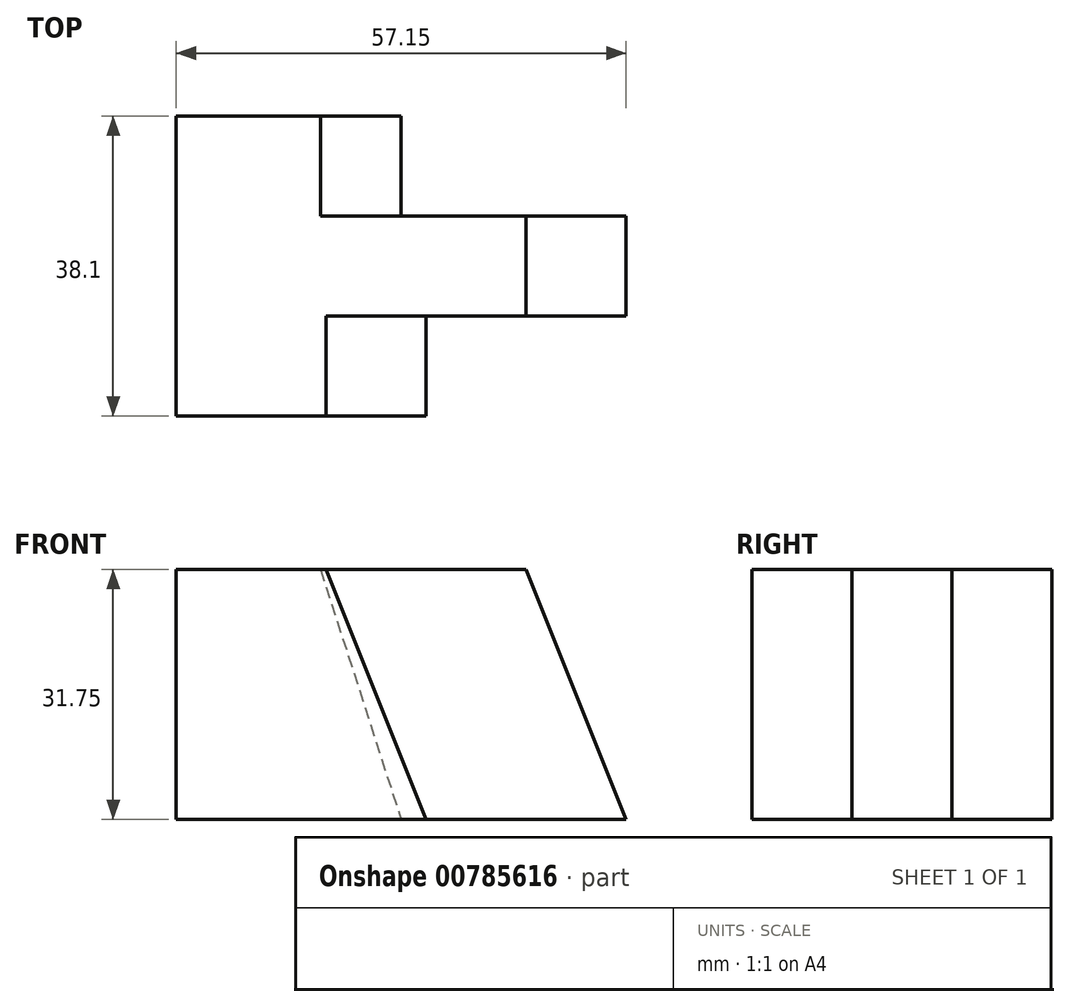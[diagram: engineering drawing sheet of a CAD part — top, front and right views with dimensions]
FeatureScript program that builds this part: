
annotation { "Feature Type Name" : "Feature", "Feature Type Description" : "" }
export const myFeature = defineFeature(function(context is Context, id is Id, definition is map)
    precondition{}
    {
        {
            var Q0;
            Q0=qCreatedBy(makeId("Front.planeOp"),FACE);
            var sketch = newSketch(context, id + "F0", { "sketchPlane" : qUnion([Q0])});
            skLineSegment(sketch, "E0", {"start": v(0, 0) * mm, "end": v(57.15, 0) * mm});
            skLineSegment(sketch, "E1", {"start": v(57.15, 0) * mm, "end": v(57.15, 31.75) * mm});
            skLineSegment(sketch, "E2", {"start": v(57.15, 31.75) * mm, "end": v(0, 31.75) * mm});
            skLineSegment(sketch, "E3", {"start": v(0, 0) * mm, "end": v(0, 31.75) * mm});
            skSolve(sketch);
        }
        {
            var Q0;
            Q0=makeQuery(id+"F0.imprint","IMPRINT",FACE,{"disambiguationData":[TD([[makeQuery(id+"F0.imprint","IMPRINT",EDGE,{"derivedFrom":sQuery(id+"F0.wireOp",EDGE,"E0")}),1.0]])]});
            extrude(context, id + "F1", {"entities" : qUnion([Q0]), "depth" : 38.1 * mm, "offsetDistance" : 25.4 * mm});
        }
        {
            var Q0;
            Q0=makeQuery(id+"F1.opExtrude","CAP_FACE",FACE,{"disambiguationData":[OSD([sQuery(id+"F0.wireOp",EDGE,"E0"),sQuery(id+"F0.wireOp",EDGE,"E1"),sQuery(id+"F0.wireOp",EDGE,"E2"),sQuery(id+"F0.wireOp",EDGE,"E3")])],"isStart":false});
            var sketch = newSketch(context, id + "F2", { "sketchPlane" : qUnion([Q0])});
            skLineSegment(sketch, "E4", {"start": v(19.05, 31.75) * mm, "end": v(31.75, 0) * mm});
            skLineSegment(sketch, "E5", {"start": v(19.05, 31.75) * mm, "end": v(57.15, 31.75) * mm});
            skLineSegment(sketch, "E6", {"start": v(31.75, 0) * mm, "end": v(57.15, 0) * mm});
            skLineSegment(sketch, "E7", {"start": v(57.15, 0) * mm, "end": v(57.15, 31.75) * mm});
            skSolve(sketch);
        }
        {
            var Q0;
            Q0=makeQuery(id+"F2.imprint","IMPRINT",FACE,{"disambiguationData":[TD([[makeQuery(id+"F2.imprint","IMPRINT",EDGE,{"derivedFrom":sQuery(id+"F2.wireOp",EDGE,"E4")}),1.0]])]});
            extrude(context, id + "F3", {"entities" : qUnion([Q0]), "operationType" : NewBodyOperationType.REMOVE, "oppositeDirection" : true, "depth" : 12.7 * mm, "offsetDistance" : 25.4 * mm});
        }
        {
            var Q0;
            Q0=makeQuery(id+"F3.boolean.opBoolean","COPY",FACE,{"derivedFrom":makeQuery(id+"F3.opExtrude","CAP_FACE",FACE,{"disambiguationData":[OSD([sQuery(id+"F2.wireOp",EDGE,"E4"),sQuery(id+"F2.wireOp",EDGE,"E5"),sQuery(id+"F2.wireOp",EDGE,"E6"),sQuery(id+"F2.wireOp",EDGE,"E7")])],"isStart":false})});
            var sketch = newSketch(context, id + "F4", { "sketchPlane" : qUnion([Q0])});
            skLineSegment(sketch, "E8", {"start": v(19.05, 31.75) * mm, "end": v(44.45, 31.75) * mm});
            skLineSegment(sketch, "E9", {"start": v(44.45, 31.75) * mm, "end": v(57.15, 0) * mm});
            skLineSegment(sketch, "E10", {"start": v(57.15, 0) * mm, "end": v(57.15, 31.75) * mm});
            skLineSegment(sketch, "E11", {"start": v(57.15, 31.75) * mm, "end": v(44.45, 31.75) * mm});
            skSolve(sketch);
        }
        {
            var Q0;
            Q0=makeQuery(id+"F4.imprint","IMPRINT",FACE,{"disambiguationData":[TD([[makeQuery(id+"F4.imprint","IMPRINT",EDGE,{"derivedFrom":sQuery(id+"F4.wireOp",EDGE,"E9")}),1.0]])]});
            extrude(context, id + "F5", {"entities" : qUnion([Q0]), "operationType" : NewBodyOperationType.REMOVE, "oppositeDirection" : true, "depth" : 25.4 * mm, "offsetDistance" : 25.4 * mm});
        }
        {
            var Q0;
            Q0=makeQuery(id+"F1.opExtrude","CAP_FACE",FACE,{"disambiguationData":[OSD([sQuery(id+"F0.wireOp",EDGE,"E0"),sQuery(id+"F0.wireOp",EDGE,"E1"),sQuery(id+"F0.wireOp",EDGE,"E2"),sQuery(id+"F0.wireOp",EDGE,"E3")])],"isStart":true});
            var sketch = newSketch(context, id + "F6", { "sketchPlane" : qUnion([Q0])});
            skLineSegment(sketch, "E12", {"start": v(0, 31.75) * mm, "end": v(-18.33, 31.75) * mm});
            skLineSegment(sketch, "E13", {"start": v(-18.33, 31.75) * mm, "end": v(-28.58, 0) * mm});
            skLineSegment(sketch, "E14", {"start": v(-18.33, 31.75) * mm, "end": v(-44.45, 31.75) * mm});
            skLineSegment(sketch, "E15", {"start": v(-44.45, 31.75) * mm, "end": v(-57.15, 0) * mm});
            skLineSegment(sketch, "E16", {"start": v(-57.15, 0) * mm, "end": v(-28.58, 0) * mm});
            skSolve(sketch);
        }
        {
            var Q0;
            Q0=makeQuery(id+"F6.imprint","IMPRINT",FACE,{"disambiguationData":[TD([[makeQuery(id+"F6.imprint","IMPRINT",EDGE,{"derivedFrom":sQuery(id+"F6.wireOp",EDGE,"E13")}),-1.0]])]});
            extrude(context, id + "F7", {"entities" : qUnion([Q0]), "operationType" : NewBodyOperationType.REMOVE, "oppositeDirection" : true, "depth" : 12.7 * mm, "offsetDistance" : 25.4 * mm});
        }
    });
